SOLIDWORKS PART (.sldprt)
format: sldprt  version: not decoded by parser v0  size: 92,672 bytes
history: native  units: mm
features: sketch x3, extrude x2, material x1, cut_extrude x1 (+13 scaffold rows collapsed)
feature tree (20):
  scaffold x13  (default folders/planes/origin — collapsed)
  material  "Material <not specified>"
  sketch  "Sketch2"  dims[D1=5.0mm D2=12.0mm]
  extrude  "Boss-Extrude1"  Depth=15mm
  sketch  "Sketch3"  dims[D1=5.0mm D2=12.0mm]
  extrude  "Boss-Extrude2"  [1 undecoded]
  sketch  "Sketch4"  dims[c1.D1=5.0mm c1.D2=12.0mm c2.D1=~11.723563mm c2.D2=~20.29811mm]
  cut_extrude  "Cut-Extrude1"  Depth=7.1mm
decode coverage: 5 of 6 modeling features carry decoded parameters
note: ~ marks probable driven/reference dimensions
note: 1 parameter value undecoded
note: suppression state not decoded; provenance and decode notes live in map.json
